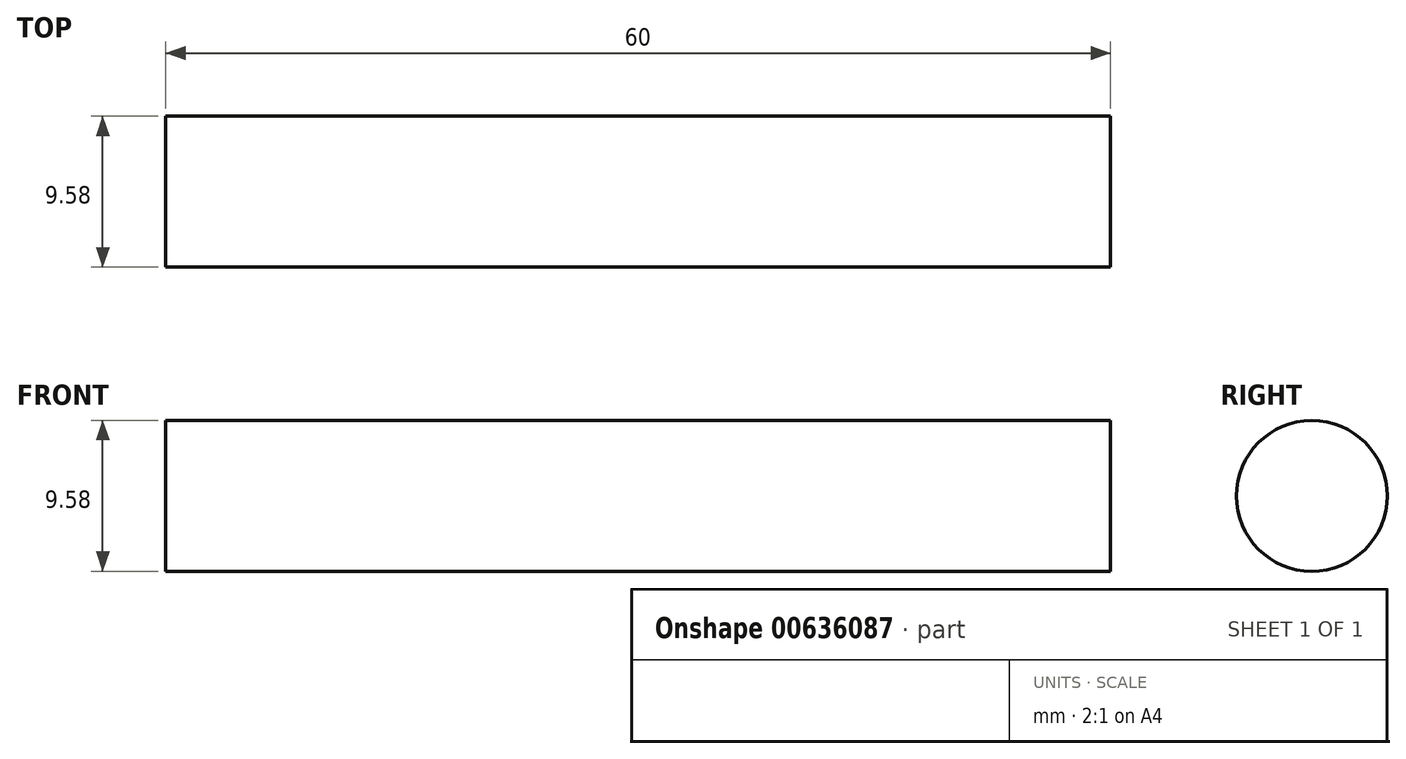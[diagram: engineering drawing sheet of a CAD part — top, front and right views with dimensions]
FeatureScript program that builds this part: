
annotation { "Feature Type Name" : "Feature", "Feature Type Description" : "" }
export const myFeature = defineFeature(function(context is Context, id is Id, definition is map)
    precondition{}
    {
        {
            var Q0;
            Q0=qCreatedBy(makeId("Right.planeOp"),FACE);
            var sketch = newSketch(context, id + "F0", { "sketchPlane" : qUnion([Q0])});
            skCircle(sketch, "E0", {"center": v(0, 0) * mm, "radius": 4.8 * mm});
            skSolve(sketch);
        }
        {
            var Q0;
            Q0 = qSketchRegion(id + "F0", true);
            extrude(context, id + "F1", {"entities" : qUnion([Q0]), "depth" : 60 * mm, "offsetDistance" : 25 * mm});
        }
    });
